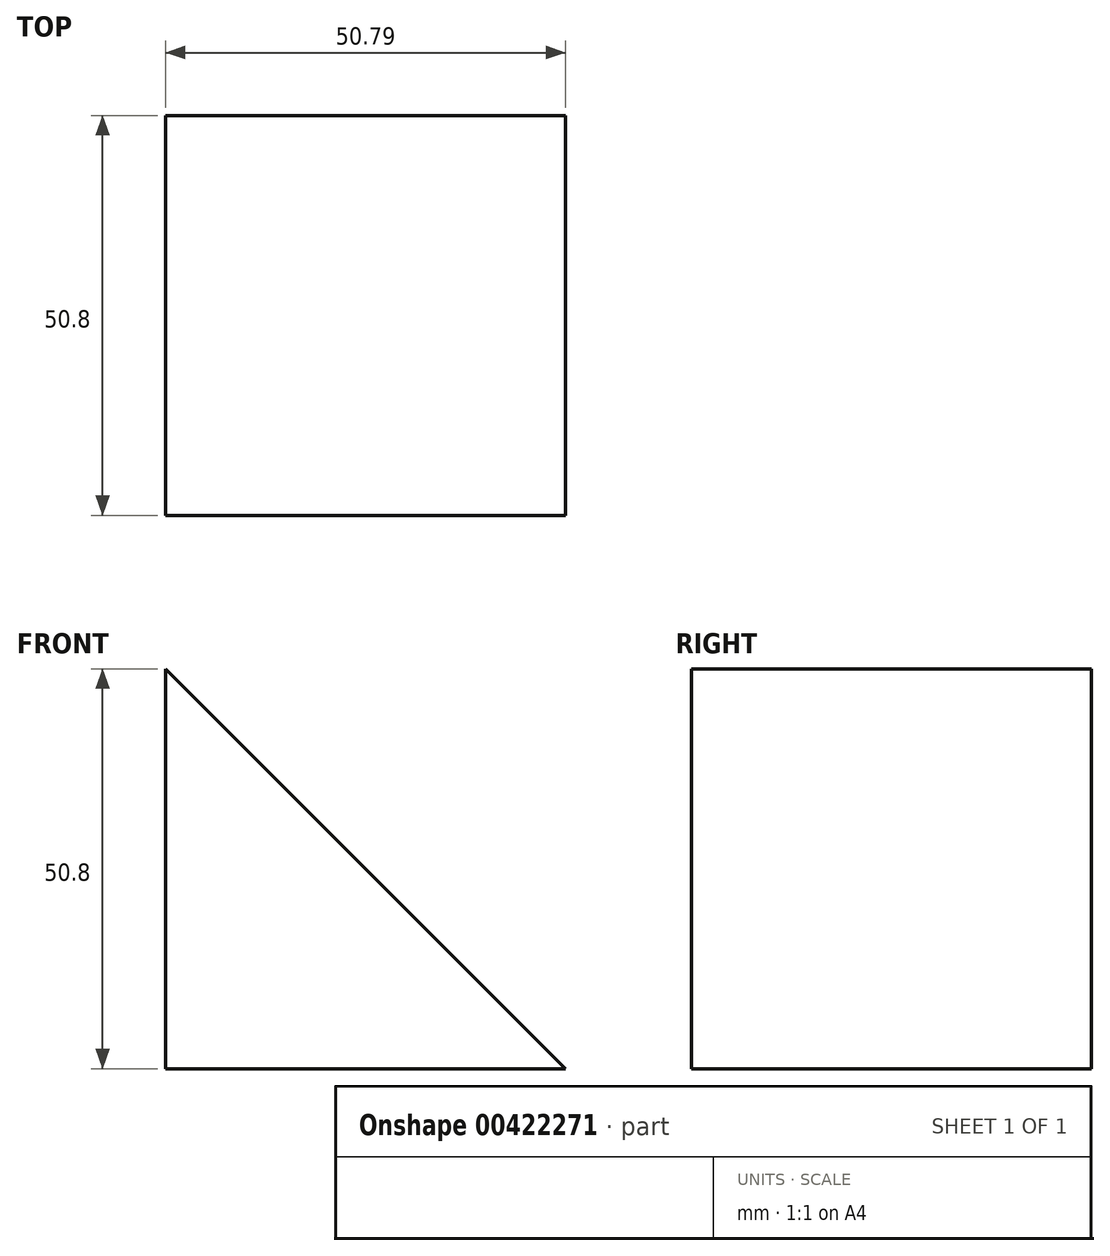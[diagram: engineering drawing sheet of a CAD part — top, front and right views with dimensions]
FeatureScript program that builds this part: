
annotation { "Feature Type Name" : "Feature", "Feature Type Description" : "" }
export const myFeature = defineFeature(function(context is Context, id is Id, definition is map)
    precondition{}
    {
        {
            var Q0;
            Q0=qCreatedBy(makeId("Front.planeOp"),FACE);
            var sketch = newSketch(context, id + "F0", { "sketchPlane" : qUnion([Q0])});
            skLineSegment(sketch, "E0", {"start": v(-24.63, 29.4) * mm, "end": v(-24.63, -21.39) * mm});
            skLineSegment(sketch, "E1", {"start": v(-24.63, -21.39) * mm, "end": v(26.16, -21.39) * mm});
            skLineSegment(sketch, "E2", {"start": v(26.16, -21.39) * mm, "end": v(-24.63, 29.4) * mm});
            skSolve(sketch);
        }
        {
            var Q0;
            Q0=makeQuery(id+"F0.imprint","IMPRINT",FACE,{"disambiguationData":[TD([[makeQuery(id+"F0.imprint","IMPRINT",EDGE,{"derivedFrom":sQuery(id+"F0.wireOp",EDGE,"E0")}),1.0]])]});
            extrude(context, id + "F1", {"entities" : qUnion([Q0]), "depth" : 50.8 * mm});
        }
    });
